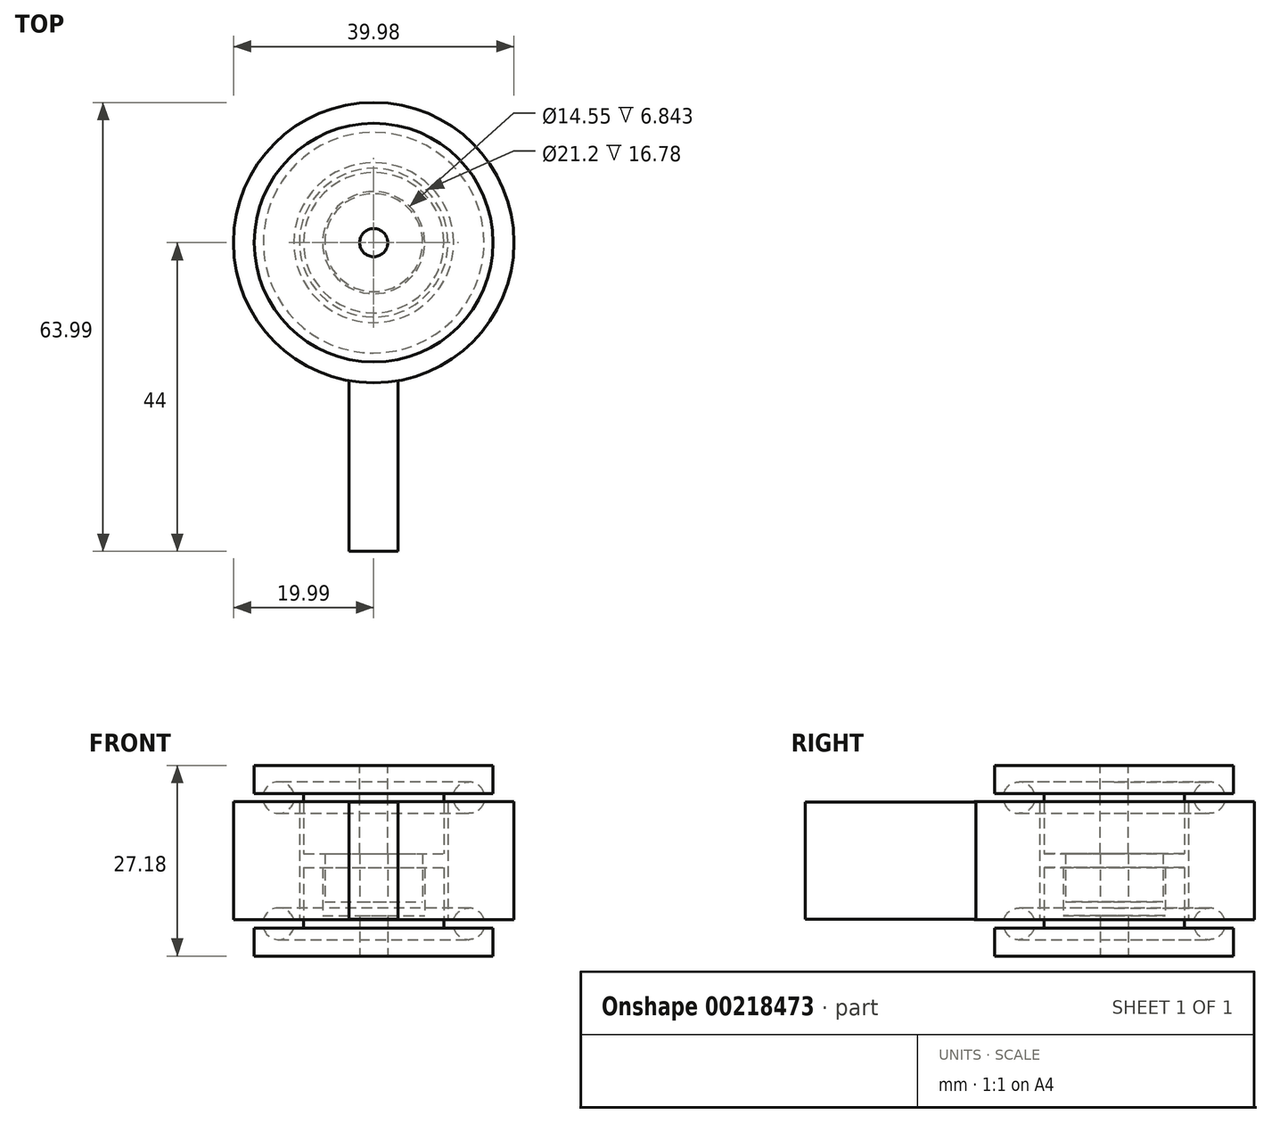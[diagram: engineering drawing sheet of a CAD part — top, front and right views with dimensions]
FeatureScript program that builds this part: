
annotation { "Feature Type Name" : "Feature", "Feature Type Description" : "" }
export const myFeature = defineFeature(function(context is Context, id is Id, definition is map)
    precondition{}
    {
        {
            var Q0;
            Q0=qCreatedBy(makeId("Front.planeOp"),FACE);
            var sketch = newSketch(context, id + "F0", { "sketchPlane" : qUnion([Q0])});
            skLineSegment(sketch, "E0", {"start": v(-17.02, 0) * mm, "end": v(-2, 0) * mm});
            skLineSegment(sketch, "E1", {"start": v(-17.02, 4) * mm, "end": v(-17.02, 0) * mm});
            skLineSegment(sketch, "E2.trimOffspring", {"start": v(-7.27, 12.59) * mm, "end": v(-10, 12.59) * mm});
            skPoint(sketch, "E3.orphan", {"position": v(0, 0) * mm});
            skLineSegment(sketch, "E4", {"start": v(-17.02, 4) * mm, "end": v(-15.74, 4) * mm});
            skLineSegment(sketch, "E5", {"start": v(-2, 5.75) * mm, "end": v(-2, 0) * mm});
            skLineSegment(sketch, "E6", {"start": v(0, 0) * mm, "end": v(0, 29.99) * mm, "construction": true});
            skLineSegment(sketch, "E7", {"start": v(-27.75, 4.6) * mm, "end": v(8.62, 4.6) * mm, "construction": true});
            skArc(sketch, "E8", {"start": v(-11.4, 5.2) * mm, "mid": v(-13.57, 6.85) * mm, "end": v(-15.74, 5.2) * mm});
            skLineSegment(sketch, "E9", {"start": v(-10, 12.59) * mm, "end": v(-10, 4) * mm});
            skLineSegment(sketch, "E10", {"start": v(-27.88, 13.59) * mm, "end": v(8.7, 13.59) * mm, "construction": true});
            skLineSegment(sketch, "E11.bottom", {"start": v(-10.6, 5.2) * mm, "end": v(-11.4, 5.2) * mm});
            skLineSegment(sketch, "E11.top", {"start": v(-10.6, 21.98) * mm, "end": v(-11.4, 21.98) * mm});
            skLineSegment(sketch, "E11.left", {"start": v(-10.6, 5.2) * mm, "end": v(-10.6, 21.98) * mm});
            skLineSegment(sketch, "E11.right", {"start": v(-19.99, 5.2) * mm, "end": v(-19.99, 21.98) * mm});
            skPoint(sketch, "E11.middle", {"position": v(-15.3, 13.59) * mm});
            skArc(sketch, "E12.trimOffspring", {"start": v(-15.74, 4) * mm, "mid": v(-13.57, 2.35) * mm, "end": v(-11.4, 4) * mm});
            skLineSegment(sketch, "E13.trimOffspring", {"start": v(-15.74, 5.2) * mm, "end": v(-19.99, 5.2) * mm});
            skLineSegment(sketch, "E14.trimOffspring", {"start": v(-11.4, 4) * mm, "end": v(-10, 4) * mm});
            skArc(sketch, "E15.MirrorCS", {"start": v(-11.4, 21.98) * mm, "mid": v(-13.57, 20.33) * mm, "end": v(-15.74, 21.98) * mm});
            skLineSegment(sketch, "E16.MirrorCS", {"start": v(-6.97, 14.59) * mm, "end": v(-10, 14.59) * mm});
            skLineSegment(sketch, "E17.MirrorCS", {"start": v(-10, 14.59) * mm, "end": v(-10, 23.18) * mm});
            skLineSegment(sketch, "E18.MirrorCS", {"start": v(-1.99, 14.59) * mm, "end": v(-2, 27.18) * mm});
            skArc(sketch, "E19.MirrorCS", {"start": v(-15.74, 23.18) * mm, "mid": v(-13.57, 24.83) * mm, "end": v(-11.4, 23.18) * mm});
            skLineSegment(sketch, "E20.MirrorCS", {"start": v(-17.02, 23.18) * mm, "end": v(-15.74, 23.18) * mm});
            skLineSegment(sketch, "E21.MirrorCS", {"start": v(-17.02, 23.18) * mm, "end": v(-17.02, 27.18) * mm});
            skLineSegment(sketch, "E22.MirrorCS", {"start": v(-17.02, 27.18) * mm, "end": v(-2, 27.18) * mm});
            skLineSegment(sketch, "E23.MirrorCS", {"start": v(-11.4, 23.18) * mm, "end": v(-10, 23.18) * mm});
            skLineSegment(sketch, "E24.trimOffspring", {"start": v(-15.74, 21.98) * mm, "end": v(-19.99, 21.98) * mm});
            skLineSegment(sketch, "E25", {"start": v(-7.27, 12.59) * mm, "end": v(-7.27, 5.75) * mm});
            skLineSegment(sketch, "E26", {"start": v(-7.27, 5.75) * mm, "end": v(-2, 5.75) * mm});
            skLineSegment(sketch, "E27.0", {"start": v(-6.97, 12.59) * mm, "end": v(-6.97, 7.75) * mm});
            skLineSegment(sketch, "E28.0", {"start": v(-6.97, 7.75) * mm, "end": v(-2, 7.75) * mm});
            skLineSegment(sketch, "E29", {"start": v(-6.97, 12.59) * mm, "end": v(-6.97, 14.59) * mm});
            skLineSegment(sketch, "E30", {"start": v(-2, 7.75) * mm, "end": v(-1.99, 14.59) * mm});
            skSolve(sketch);
        }
        {
            var Q0;
            Q0=makeQuery(id+"F0.imprint","IMPRINT",FACE,{"disambiguationData":[TD([[makeQuery(id+"F0.imprint","IMPRINT",EDGE,{"derivedFrom":sQuery(id+"F0.wireOp",EDGE,"E16.MirrorCS")}),-1.0]])]});
            var Q1;
            Q1=makeQuery(id+"F0.imprint","IMPRINT",FACE,{"disambiguationData":[TD([[makeQuery(id+"F0.imprint","IMPRINT",EDGE,{"derivedFrom":sQuery(id+"F0.wireOp",EDGE,"E8")}),-1.0]])]});
            var Q2;
            Q2=makeQuery(id+"F0.imprint","IMPRINT",FACE,{"disambiguationData":[TD([[makeQuery(id+"F0.imprint","IMPRINT",EDGE,{"derivedFrom":sQuery(id+"F0.wireOp",EDGE,"E0")}),1.0]])]});
            var Q3;
            Q3=sQuery(id+"F0.wireOp",EDGE,"E6");
            revolve(context, id + "F1", {"entities" : qUnion([Q0, Q1, Q2]), "axis" : qUnion([Q3]), "revolveType" : RevolveType.FULL});
        }
        {
            var Q0;
            Q0=qCreatedBy(makeId("Front.planeOp"),FACE);
            cPlane(context, id + "F2", {"entities" : qUnion([Q0]), "cplaneType" : CPlaneType.OFFSET, "offset" : 19 * mm, "width" : 150 * mm, "height" : 150 * mm});
        }
        {
            var Q0;
            Q0=qCreatedBy(id+"F2.planeOp",FACE);
            var sketch = newSketch(context, id + "F3", { "sketchPlane" : qUnion([Q0])});
            skLineSegment(sketch, "E31.bottom", {"start": v(3.5, 5.22) * mm, "end": v(-3.5, 5.22) * mm});
            skLineSegment(sketch, "E31.top", {"start": v(3.5, 21.94) * mm, "end": v(-3.5, 21.94) * mm});
            skLineSegment(sketch, "E31.left", {"start": v(3.5, 5.22) * mm, "end": v(3.5, 21.94) * mm});
            skLineSegment(sketch, "E31.right", {"start": v(-3.5, 5.22) * mm, "end": v(-3.5, 21.94) * mm});
            skPoint(sketch, "E31.middle", {"position": v(0, 13.58) * mm});
            skSolve(sketch);
        }
        {
            var Q0;
            Q0=makeQuery(id+"F3.imprint","IMPRINT",FACE,{"disambiguationData":[TD([[makeQuery(id+"F3.imprint","IMPRINT",EDGE,{"derivedFrom":sQuery(id+"F3.wireOp",EDGE,"E31.bottom")}),-1.0]])]});
            extrude(context, id + "F4", {"entities" : qUnion([Q0]), "operationType" : NewBodyOperationType.ADD, "depth" : 25 * mm});
        }
    });
